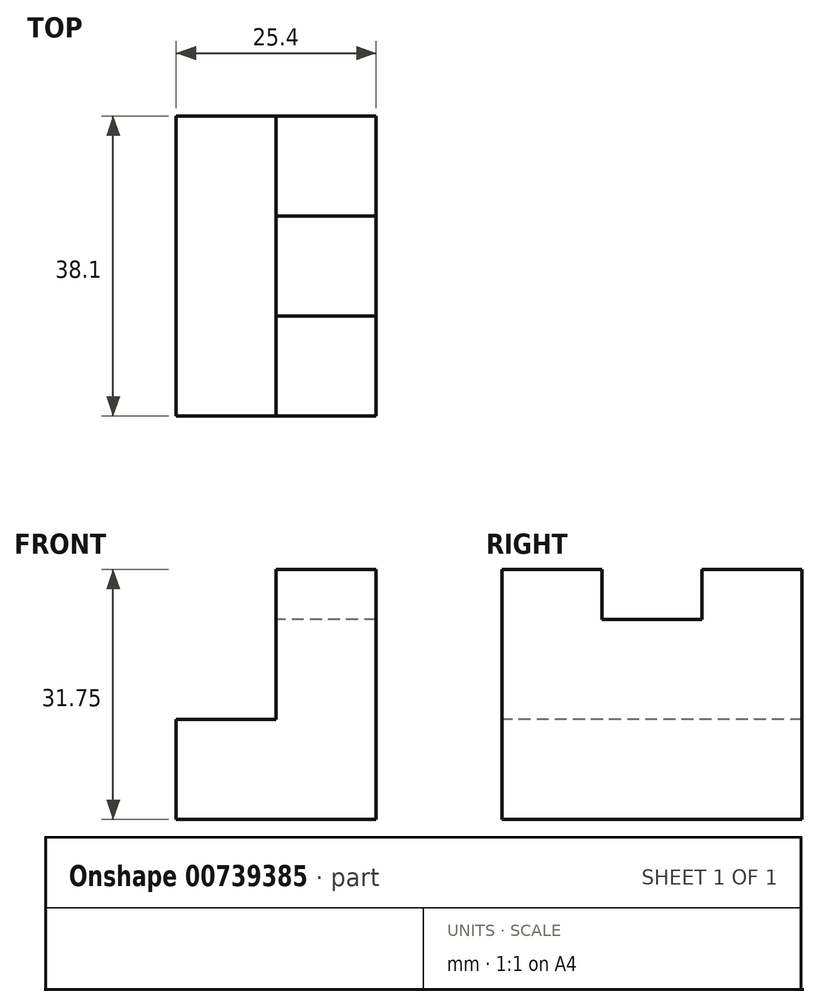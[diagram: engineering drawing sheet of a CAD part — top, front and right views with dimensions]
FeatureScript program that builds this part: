
annotation { "Feature Type Name" : "Feature", "Feature Type Description" : "" }
export const myFeature = defineFeature(function(context is Context, id is Id, definition is map)
    precondition{}
    {
        {
            var Q0;
            Q0=qCreatedBy(makeId("Front.planeOp"),FACE);
            var sketch = newSketch(context, id + "F0", { "sketchPlane" : qUnion([Q0])});
            skLineSegment(sketch, "E0", {"start": v(0, 0) * mm, "end": v(25.4, 0) * mm});
            skLineSegment(sketch, "E1", {"start": v(25.4, 0) * mm, "end": v(25.4, 31.75) * mm});
            skLineSegment(sketch, "E2", {"start": v(25.4, 31.75) * mm, "end": v(12.7, 31.75) * mm});
            skLineSegment(sketch, "E3", {"start": v(12.7, 31.75) * mm, "end": v(12.7, 12.7) * mm});
            skLineSegment(sketch, "E4", {"start": v(12.7, 12.7) * mm, "end": v(0, 12.7) * mm});
            skLineSegment(sketch, "E5", {"start": v(0, 12.7) * mm, "end": v(0, 0) * mm});
            skSolve(sketch);
        }
        {
            var Q0;
            Q0=makeQuery(id+"F0.imprint","IMPRINT",FACE,{"disambiguationData":[TD([[makeQuery(id+"F0.imprint","IMPRINT",EDGE,{"derivedFrom":sQuery(id+"F0.wireOp",EDGE,"E0")}),1.0]])]});
            extrude(context, id + "F1", {"entities" : qUnion([Q0]), "oppositeDirection" : true, "depth" : 38.1 * mm, "offsetDistance" : 25.4 * mm});
        }
        {
            var Q0;
            Q0=makeQuery(id+"F1.opExtrude","SWEPT_FACE",FACE,{"disambiguationData":[OSD([sQuery(id+"F0.wireOp",EDGE,"E3")])]});
            var sketch = newSketch(context, id + "F2", { "sketchPlane" : qUnion([Q0])});
            skLineSegment(sketch, "E6", {"start": v(-25.4, 31.75) * mm, "end": v(-25.4, 25.4) * mm});
            skLineSegment(sketch, "E7", {"start": v(-25.4, 25.4) * mm, "end": v(-12.7, 25.4) * mm});
            skLineSegment(sketch, "E8", {"start": v(-12.7, 25.4) * mm, "end": v(-12.7, 31.75) * mm});
            skLineSegment(sketch, "E9", {"start": v(-12.7, 31.75) * mm, "end": v(-25.4, 31.75) * mm});
            skSolve(sketch);
        }
        {
            var Q0;
            Q0=makeQuery(id+"F2.imprint","IMPRINT",FACE,{"disambiguationData":[TD([[makeQuery(id+"F2.imprint","IMPRINT",EDGE,{"derivedFrom":sQuery(id+"F2.wireOp",EDGE,"E6")}),1.0]])]});
            extrude(context, id + "F3", {"entities" : qUnion([Q0]), "operationType" : NewBodyOperationType.REMOVE, "oppositeDirection" : true, "depth" : 50.8 * mm, "offsetDistance" : 25.4 * mm});
        }
    });
